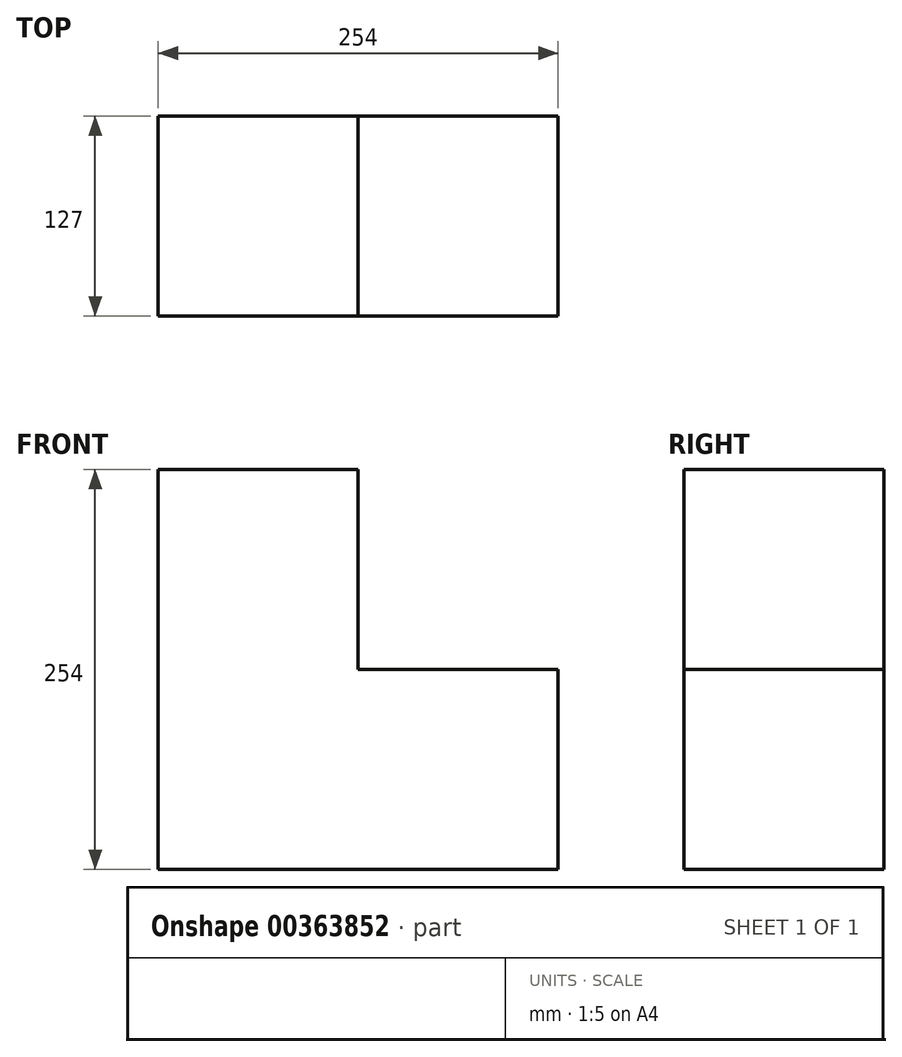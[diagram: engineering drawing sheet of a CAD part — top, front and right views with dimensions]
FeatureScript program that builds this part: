
annotation { "Feature Type Name" : "Feature", "Feature Type Description" : "" }
export const myFeature = defineFeature(function(context is Context, id is Id, definition is map)
    precondition{}
    {
        {
            var Q0;
            Q0=qCreatedBy(makeId("Front.planeOp"),FACE);
            var sketch = newSketch(context, id + "F0", { "sketchPlane" : qUnion([Q0])});
            skLineSegment(sketch, "E0.top", {"start": v(-63.5, 18.33) * mm, "end": v(63.5, 18.33) * mm});
            skLineSegment(sketch, "E0.left", {"start": v(-63.5, 145.33) * mm, "end": v(-63.5, 18.33) * mm});
            skPoint(sketch, "E0.middle", {"position": v(0, 81.83) * mm});
            skLineSegment(sketch, "E1.bottom", {"start": v(-63.5, 145.33) * mm, "end": v(-190.5, 145.33) * mm});
            skLineSegment(sketch, "E1.right", {"start": v(-190.5, 145.33) * mm, "end": v(-190.5, 18.33) * mm});
            skLineSegment(sketch, "E2.top", {"start": v(-190.5, -108.67) * mm, "end": v(63.5, -108.67) * mm});
            skLineSegment(sketch, "E2.left", {"start": v(-190.5, 18.33) * mm, "end": v(-190.5, -108.67) * mm});
            skLineSegment(sketch, "E2.right", {"start": v(63.5, 18.33) * mm, "end": v(63.5, -108.67) * mm});
            skPoint(sketch, "E0.right.start.orphan", {"position": v(63.5, 145.33) * mm});
            skSolve(sketch);
        }
        {
            var Q0;
            Q0=makeQuery(id+"F0.imprint","IMPRINT",FACE,{"disambiguationData":[TD([[makeQuery(id+"F0.imprint","IMPRINT",EDGE,{"derivedFrom":sQuery(id+"F0.wireOp",EDGE,"E1.bottom")}),1.0]])]});
            extrude(context, id + "F1", {"entities" : qUnion([Q0]), "endBound" : BoundingType.SYMMETRIC, "depth" : 127 * mm});
        }
    });
